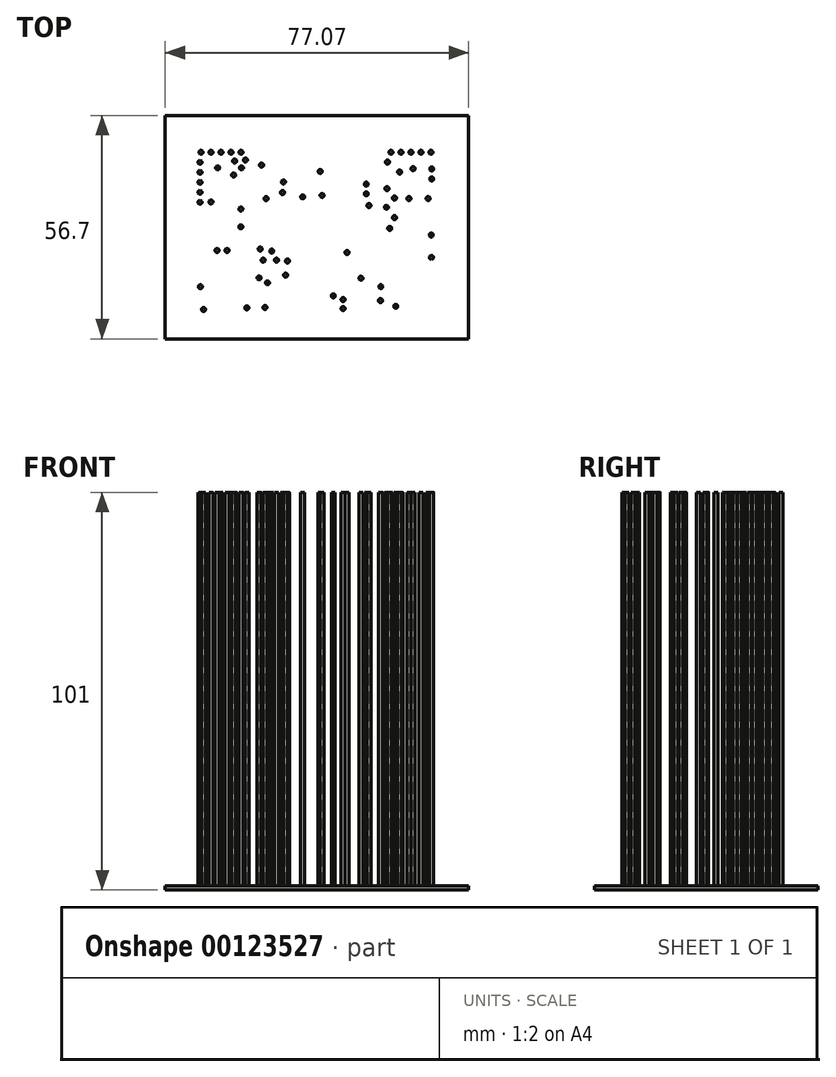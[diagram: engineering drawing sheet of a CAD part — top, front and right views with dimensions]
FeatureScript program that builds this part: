
annotation { "Feature Type Name" : "Feature", "Feature Type Description" : "" }
export const myFeature = defineFeature(function(context is Context, id is Id, definition is map)
    precondition{}
    {
        {
            var Q0;
            Q0=qCreatedBy(makeId("Top.planeOp"),FACE);
            var sketch = newSketch(context, id + "F0", { "sketchPlane" : qUnion([Q0])});
            skCircle(sketch, "E0", {"center": v(-18.67, -0.39) * mm, "radius": 0.5 * mm});
            skCircle(sketch, "E1", {"center": v(-17.98, 9.7) * mm, "radius": 0.5 * mm});
            skCircle(sketch, "E2", {"center": v(-19.89, 2.35) * mm, "radius": 0.5 * mm});
            skCircle(sketch, "E3", {"center": v(-23.55, 7.2) * mm, "radius": 0.5 * mm});
            skCircle(sketch, "E4", {"center": v(-19.88, 7.33) * mm, "radius": 0.5 * mm});
            skCircle(sketch, "E5", {"center": v(-18.98, 18.95) * mm, "radius": 0.5 * mm});
            skCircle(sketch, "E6", {"center": v(-26.6, 18.95) * mm, "radius": 0.5 * mm});
            skCircle(sketch, "E7", {"center": v(-21.52, 18.95) * mm, "radius": 0.5 * mm});
            skCircle(sketch, "E8", {"center": v(-29.14, 18.95) * mm, "radius": 0.5 * mm});
            skCircle(sketch, "E9", {"center": v(-24.07, 18.95) * mm, "radius": 0.5 * mm});
            skCircle(sketch, "E10", {"center": v(-18.1, 16.48) * mm, "radius": 0.5 * mm});
            skCircle(sketch, "E11", {"center": v(-4.33, -17.52) * mm, "radius": 0.5 * mm});
            skCircle(sketch, "E12", {"center": v(-6.83, -18.48) * mm, "radius": 0.5 * mm});
            skCircle(sketch, "E13", {"center": v(-24.6, 14.78) * mm, "radius": 0.5 * mm});
            skCircle(sketch, "E14", {"center": v(29.52, 16.41) * mm, "radius": 0.5 * mm});
            skCircle(sketch, "E15", {"center": v(29.52, 13.87) * mm, "radius": 0.5 * mm});
            skCircle(sketch, "E16", {"center": v(-21.2, 13.95) * mm, "radius": 0.5 * mm});
            skCircle(sketch, "E17", {"center": v(29.52, 6.25) * mm, "radius": 0.5 * mm});
            skCircle(sketch, "E18", {"center": v(-29.23, -2.08) * mm, "radius": 0.5 * mm});
            skCircle(sketch, "E19", {"center": v(-16.32, -18.73) * mm, "radius": 0.5 * mm});
            skCircle(sketch, "E20", {"center": v(3.45, 7.62) * mm, "radius": 0.5 * mm});
            skCircle(sketch, "E21", {"center": v(-6.83, -20.75) * mm, "radius": 0.5 * mm});
            skCircle(sketch, "E22", {"center": v(-29.27, -7.75) * mm, "radius": 0.5 * mm});
            skCircle(sketch, "E23", {"center": v(-11.35, -13.05) * mm, "radius": 0.5 * mm});
            skCircle(sketch, "E24", {"center": v(18, 17) * mm, "radius": 0.5 * mm});
            skCircle(sketch, "E25", {"center": v(25.05, 15) * mm, "radius": 0.5 * mm});
            skCircle(sketch, "E26", {"center": v(20.73, 16.75) * mm, "radius": 0.5 * mm});
            skCircle(sketch, "E27", {"center": v(19, 15) * mm, "radius": 0.5 * mm});
            skCircle(sketch, "E28", {"center": v(13.47, -8.45) * mm, "radius": 0.5 * mm});
            skCircle(sketch, "E29", {"center": v(10.1, -8.45) * mm, "radius": 0.5 * mm});
            skCircle(sketch, "E30", {"center": v(11.3, -6.17) * mm, "radius": 0.5 * mm});
            skCircle(sketch, "E31", {"center": v(7.78, -12.28) * mm, "radius": 0.5 * mm});
            skCircle(sketch, "E32", {"center": v(8.32, 11.43) * mm, "radius": 0.5 * mm});
            skCircle(sketch, "E33", {"center": v(8.57, 8.72) * mm, "radius": 0.5 * mm});
            skCircle(sketch, "E34", {"center": v(13.9, 15.7) * mm, "radius": 0.5 * mm});
            skCircle(sketch, "E35", {"center": v(12.72, 7.17) * mm, "radius": 0.5 * mm});
            skCircle(sketch, "E36", {"center": v(14.22, -5.62) * mm, "radius": 0.5 * mm});
            skCircle(sketch, "E37", {"center": v(21.66, 18.95) * mm, "radius": 0.5 * mm});
            skCircle(sketch, "E38", {"center": v(26.73, 18.95) * mm, "radius": 0.5 * mm});
            skCircle(sketch, "E39", {"center": v(19.11, 18.95) * mm, "radius": 0.5 * mm});
            skCircle(sketch, "E40", {"center": v(24.2, 18.95) * mm, "radius": 0.5 * mm});
            skCircle(sketch, "E41", {"center": v(29.27, 18.95) * mm, "radius": 0.5 * mm});
            skCircle(sketch, "E42", {"center": v(20.98, 13.2) * mm, "radius": 0.5 * mm});
            skCircle(sketch, "E43", {"center": v(-29.34, 12.18) * mm, "radius": 0.5 * mm});
            skCircle(sketch, "E44", {"center": v(29.52, 11.33) * mm, "radius": 0.5 * mm});
            skCircle(sketch, "E45", {"center": v(-29.34, 14.72) * mm, "radius": 0.5 * mm});
            skCircle(sketch, "E46", {"center": v(29.52, 8.79) * mm, "radius": 0.5 * mm});
            skCircle(sketch, "E47", {"center": v(-1.5, 8) * mm, "radius": 0.5 * mm});
            skCircle(sketch, "E48", {"center": v(-1, 14.1) * mm, "radius": 0.5 * mm});
            skCircle(sketch, "E49", {"center": v(-7.83, -6.5) * mm, "radius": 0.5 * mm});
            skCircle(sketch, "E50", {"center": v(-28.44, 7.2) * mm, "radius": 0.5 * mm});
            skCircle(sketch, "E51", {"center": v(26.75, 6.35) * mm, "radius": 0.5 * mm});
            skCircle(sketch, "E52", {"center": v(19.15, 4.55) * mm, "radius": 0.5 * mm});
            skCircle(sketch, "E53", {"center": v(12.38, -14.2) * mm, "radius": 0.5 * mm});
            skCircle(sketch, "E54", {"center": v(29.43, -15.2) * mm, "radius": 0.5 * mm});
            skCircle(sketch, "E55", {"center": v(28.62, -20.98) * mm, "radius": 0.5 * mm});
            skCircle(sketch, "E56", {"center": v(17.62, -20.57) * mm, "radius": 0.5 * mm});
            skCircle(sketch, "E57", {"center": v(13.03, -20.47) * mm, "radius": 0.5 * mm});
            skCircle(sketch, "E58", {"center": v(-13.38, 5.42) * mm, "radius": 0.5 * mm});
            skCircle(sketch, "E59", {"center": v(-20.2, -20.18) * mm, "radius": 0.5 * mm});
            skCircle(sketch, "E60", {"center": v(25.2, -5.97) * mm, "radius": 0.5 * mm});
            skCircle(sketch, "E61", {"center": v(22.66, -5.97) * mm, "radius": 0.5 * mm});
            skCircle(sketch, "E62", {"center": v(19.15, 0.03) * mm, "radius": 0.5 * mm});
            skCircle(sketch, "E63", {"center": v(14.5, -12.95) * mm, "radius": 0.5 * mm});
            skCircle(sketch, "E64", {"center": v(7.33, -8.68) * mm, "radius": 0.5 * mm});
            skCircle(sketch, "E65", {"center": v(-12.7, 10.85) * mm, "radius": 0.5 * mm});
            skCircle(sketch, "E66", {"center": v(-12.7, 8.4) * mm, "radius": 0.5 * mm});
            skCircle(sketch, "E67", {"center": v(-17.82, 4.97) * mm, "radius": 0.5 * mm});
            skCircle(sketch, "E68", {"center": v(-16.4, -15.18) * mm, "radius": 0.5 * mm});
            skSolve(sketch);
        }
        {
            var Q0;
            Q0=qCreatedBy(makeId("Top.planeOp"),FACE);
            var sketch = newSketch(context, id + "F1", { "sketchPlane" : qUnion([Q0])});
            skLineSegment(sketch, "E69.bottom", {"start": v(-38.71, 28.26) * mm, "end": v(38.36, 28.26) * mm});
            skLineSegment(sketch, "E69.top", {"start": v(-38.71, -28.44) * mm, "end": v(38.36, -28.44) * mm});
            skLineSegment(sketch, "E69.left", {"start": v(-38.71, 28.26) * mm, "end": v(-38.71, -28.44) * mm});
            skLineSegment(sketch, "E69.right", {"start": v(38.36, 28.26) * mm, "end": v(38.36, -28.44) * mm});
            skSolve(sketch);
        }
        {
            var Q0;
            Q0=makeQuery(id+"F1.imprint","IMPRINT",FACE,{"disambiguationData":[TD([[makeQuery(id+"F1.imprint","IMPRINT",EDGE,{"derivedFrom":sQuery(id+"F1.wireOp",EDGE,"E69.bottom")}),-1.0]])]});
            extrude(context, id + "F2", {"entities" : qUnion([Q0]), "depth" : 1 * mm});
        }
        {
            var Q0;
            Q0 = qSketchRegion(id + "F0", true);
            extrude(context, id + "F3", {"entities" : qUnion([Q0]), "operationType" : NewBodyOperationType.ADD, "oppositeDirection" : true, "depth" : 100 * mm});
        }
        {
            var Q0;
            Q0=qCreatedBy(makeId("Top.planeOp"),FACE);
            var sketch = newSketch(context, id + "F4", { "sketchPlane" : qUnion([Q0])});
            skLineSegment(sketch, "E70", {"start": v(0, 74.32) * mm, "end": v(0, -74.14) * mm, "construction": true});
            skSolve(sketch);
        }
        {
            var Q0;
            Q0=makeQuery(id+"F2.opExtrude","SWEPT_BODY",BODY,{"disambiguationData":[OSD([sQuery(id+"F1.wireOp",EDGE,"E69.bottom"),sQuery(id+"F1.wireOp",EDGE,"E69.top"),sQuery(id+"F1.wireOp",EDGE,"E69.left"),sQuery(id+"F1.wireOp",EDGE,"E69.right")])]});
            var Q1;
            Q1=sQuery(id+"F4.wireOp",EDGE,"E70");
            transform(context, id + "F5", {"entities" : qUnion([Q0]), "transformType" : TransformType.ROTATION, "transformAxis" : qUnion([Q1]), "angle" : 180 * degree, "makeCopy" : false});
        }
    });
